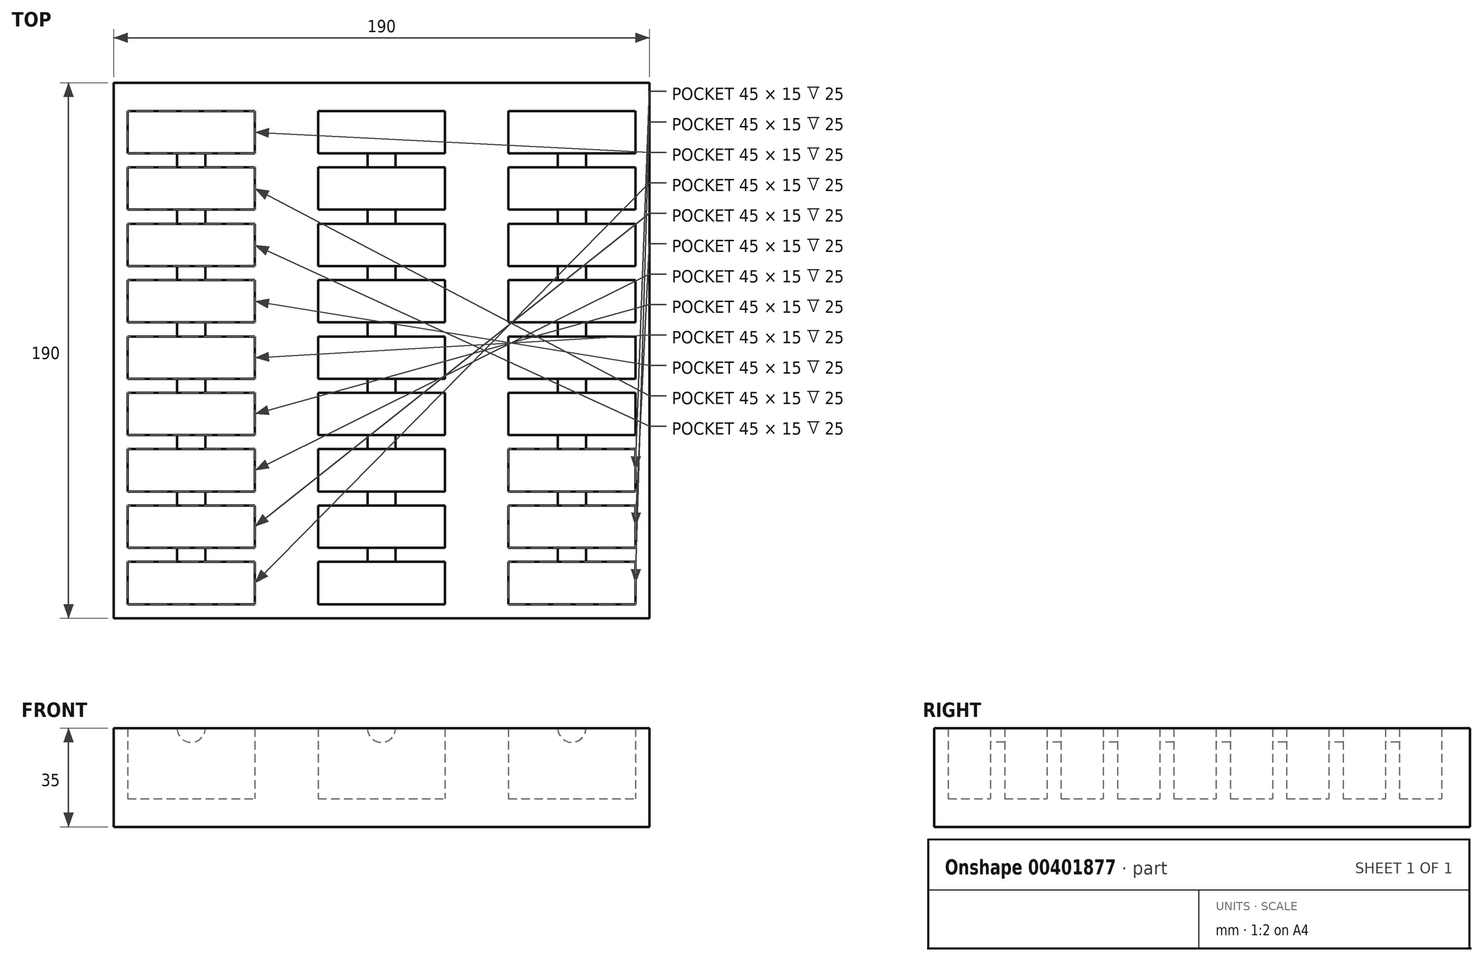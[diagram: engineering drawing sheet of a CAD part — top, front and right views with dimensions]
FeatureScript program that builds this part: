
annotation { "Feature Type Name" : "Feature", "Feature Type Description" : "" }
export const myFeature = defineFeature(function(context is Context, id is Id, definition is map)
    precondition{}
    {
        {
            var Q0;
            Q0=qCreatedBy(makeId("Top.planeOp"),FACE);
            var sketch = newSketch(context, id + "F0", { "sketchPlane" : qUnion([Q0])});
            skLineSegment(sketch, "E0.bottom", {"start": v(-95, 95) * mm, "end": v(95, 95) * mm});
            skLineSegment(sketch, "E0.top", {"start": v(-95, -95) * mm, "end": v(95, -95) * mm});
            skLineSegment(sketch, "E0.left", {"start": v(-95, 95) * mm, "end": v(-95, -95) * mm});
            skLineSegment(sketch, "E0.right", {"start": v(95, 95) * mm, "end": v(95, -95) * mm});
            skPoint(sketch, "E0.middle", {"position": v(0, 0) * mm});
            skSolve(sketch);
        }
        {
            var Q0;
            Q0 = qSketchRegion(id + "F0", true);
            extrude(context, id + "F1", {"entities" : qUnion([Q0]), "depth" : 35 * mm});
        }
        {
            var Q0;
            Q0=makeQuery(id+"F1.opExtrude","CAP_FACE",FACE,{"disambiguationData":[OSD([sQuery(id+"F0.wireOp",EDGE,"E0.bottom"),sQuery(id+"F0.wireOp",EDGE,"E0.top"),sQuery(id+"F0.wireOp",EDGE,"E0.left"),sQuery(id+"F0.wireOp",EDGE,"E0.right")])],"isStart":false});
            var sketch = newSketch(context, id + "F2", { "sketchPlane" : qUnion([Q0])});
            skLineSegment(sketch, "E1.bottom", {"start": v(90, 90) * mm, "end": v(-90, 90) * mm});
            skLineSegment(sketch, "E1.top", {"start": v(90, -90) * mm, "end": v(-90, -90) * mm});
            skLineSegment(sketch, "E1.left", {"start": v(90, 90) * mm, "end": v(90, -90) * mm});
            skLineSegment(sketch, "E1.right", {"start": v(-90, 90) * mm, "end": v(-90, -90) * mm});
            skPoint(sketch, "E1.middle", {"position": v(0, 0) * mm});
            skSolve(sketch);
        }
        {
            var Q0;
            Q0 = qSketchRegion(id + "F2", true);
            extrude(context, id + "F3", {"entities" : qUnion([Q0]), "operationType" : NewBodyOperationType.REMOVE, "oppositeDirection" : true, "depth" : 25 * mm});
        }
        {
            var Q0;
            Q0=makeQuery(id+"F3.boolean.opBoolean","COPY",FACE,{"derivedFrom":makeQuery(id+"F3.opExtrude","CAP_FACE",FACE,{"disambiguationData":[OSD([sQuery(id+"F2.wireOp",EDGE,"E1.bottom"),sQuery(id+"F2.wireOp",EDGE,"E1.top"),sQuery(id+"F2.wireOp",EDGE,"E1.left"),sQuery(id+"F2.wireOp",EDGE,"E1.right")])],"isStart":false})});
            var sketch = newSketch(context, id + "F4", { "sketchPlane" : qUnion([Q0])});
            skLineSegment(sketch, "E2.top", {"start": v(-90, -75) * mm, "end": v(-45, -75) * mm});
            skLineSegment(sketch, "E2.right", {"start": v(-45, -90) * mm, "end": v(-45, -75) * mm});
            skLineSegment(sketch, "E3.0", {"start": v(-40, -90) * mm, "end": v(-40, -70) * mm});
            skLineSegment(sketch, "E3.1", {"start": v(-90, -70) * mm, "end": v(-40, -70) * mm});
            skLineSegment(sketch, "E4", {"start": v(-45, -90) * mm, "end": v(-40, -90) * mm});
            skLineSegment(sketch, "E5", {"start": v(-90, -75) * mm, "end": v(-90, -70) * mm});
            skLineSegment(sketch, "E6", {"start": v(-45, -70) * mm, "end": v(-45, -55) * mm});
            skLineSegment(sketch, "E7", {"start": v(-45, -55) * mm, "end": v(-90, -55) * mm});
            skLineSegment(sketch, "E8.0", {"start": v(-40, -50) * mm, "end": v(-90, -50) * mm});
            skLineSegment(sketch, "E8.1", {"start": v(-40, -70) * mm, "end": v(-40, -50) * mm});
            skLineSegment(sketch, "E9", {"start": v(-90, -50) * mm, "end": v(-90, -55) * mm});
            skLineSegment(sketch, "E10", {"start": v(-45, -50) * mm, "end": v(-45, -35) * mm});
            skLineSegment(sketch, "E11", {"start": v(-45, -35) * mm, "end": v(-90, -35) * mm});
            skLineSegment(sketch, "E12.0", {"start": v(-40, -30) * mm, "end": v(-90, -30) * mm});
            skLineSegment(sketch, "E12.1", {"start": v(-40, -50) * mm, "end": v(-40, -30) * mm});
            skLineSegment(sketch, "E13", {"start": v(-90, -30) * mm, "end": v(-90, -35) * mm});
            skLineSegment(sketch, "E14", {"start": v(-45, -30) * mm, "end": v(-45, -15) * mm});
            skLineSegment(sketch, "E15", {"start": v(-45, -15) * mm, "end": v(-90, -15) * mm});
            skLineSegment(sketch, "E16.0", {"start": v(-40, -10) * mm, "end": v(-90, -10) * mm});
            skLineSegment(sketch, "E16.1", {"start": v(-40, -30) * mm, "end": v(-40, -10) * mm});
            skLineSegment(sketch, "E17", {"start": v(-90, -10) * mm, "end": v(-90, -15) * mm});
            skLineSegment(sketch, "E18", {"start": v(-45, -10) * mm, "end": v(-45, 5) * mm});
            skLineSegment(sketch, "E19", {"start": v(-45, 5) * mm, "end": v(-90, 5) * mm});
            skLineSegment(sketch, "E20.0", {"start": v(-40, 10) * mm, "end": v(-90, 10) * mm});
            skLineSegment(sketch, "E20.1", {"start": v(-40, -10) * mm, "end": v(-40, 10) * mm});
            skLineSegment(sketch, "E21", {"start": v(-90, 10) * mm, "end": v(-90, 5) * mm});
            skLineSegment(sketch, "E22", {"start": v(-45, 10) * mm, "end": v(-45, 25) * mm});
            skLineSegment(sketch, "E23", {"start": v(-45, 25) * mm, "end": v(-90, 25) * mm});
            skLineSegment(sketch, "E24.0", {"start": v(-40, 30) * mm, "end": v(-90, 30) * mm});
            skLineSegment(sketch, "E24.1", {"start": v(-40, 10) * mm, "end": v(-40, 30) * mm});
            skLineSegment(sketch, "E25", {"start": v(-90, 30) * mm, "end": v(-90, 25) * mm});
            skLineSegment(sketch, "E26", {"start": v(-45, 30) * mm, "end": v(-45, 45) * mm});
            skLineSegment(sketch, "E27", {"start": v(-45, 45) * mm, "end": v(-90, 45) * mm});
            skLineSegment(sketch, "E28.0", {"start": v(-40, 50) * mm, "end": v(-90, 50) * mm});
            skLineSegment(sketch, "E28.1", {"start": v(-40, 30) * mm, "end": v(-40, 50) * mm});
            skLineSegment(sketch, "E29", {"start": v(-90, 50) * mm, "end": v(-90, 45) * mm});
            skLineSegment(sketch, "E30", {"start": v(-45, 50) * mm, "end": v(-45, 65) * mm});
            skLineSegment(sketch, "E31", {"start": v(-45, 65) * mm, "end": v(-90, 65) * mm});
            skLineSegment(sketch, "E32.0", {"start": v(-40, 70) * mm, "end": v(-90, 70) * mm});
            skLineSegment(sketch, "E32.1", {"start": v(-40, 50) * mm, "end": v(-40, 70) * mm});
            skLineSegment(sketch, "E33", {"start": v(-90, 70) * mm, "end": v(-90, 65) * mm});
            skLineSegment(sketch, "E34", {"start": v(-45, 70) * mm, "end": v(-45, 85) * mm});
            skLineSegment(sketch, "E35", {"start": v(-45, 85) * mm, "end": v(-90, 85) * mm});
            skLineSegment(sketch, "E36", {"start": v(-40, 70) * mm, "end": v(-40, 90) * mm});
            skLineSegment(sketch, "E37", {"start": v(-40, 90) * mm, "end": v(-90, 90) * mm});
            skLineSegment(sketch, "E38", {"start": v(-90, 90) * mm, "end": v(-90, 85) * mm});
            skLineSegment(sketch, "E39.MirrorCS", {"start": v(40, 70) * mm, "end": v(40, 90) * mm});
            skLineSegment(sketch, "E40.MirrorCS", {"start": v(40, 90) * mm, "end": v(90, 90) * mm});
            skLineSegment(sketch, "E41.MirrorCS", {"start": v(90, 90) * mm, "end": v(90, 85) * mm});
            skLineSegment(sketch, "E42.MirrorCS", {"start": v(45, 85) * mm, "end": v(90, 85) * mm});
            skLineSegment(sketch, "E43.MirrorCS", {"start": v(45, 70) * mm, "end": v(45, 85) * mm});
            skLineSegment(sketch, "E44.MirrorCS", {"start": v(40, 70) * mm, "end": v(90, 70) * mm});
            skLineSegment(sketch, "E45.MirrorCS", {"start": v(90, 70) * mm, "end": v(90, 65) * mm});
            skLineSegment(sketch, "E46.MirrorCS", {"start": v(45, 65) * mm, "end": v(90, 65) * mm});
            skLineSegment(sketch, "E47.MirrorCS", {"start": v(40, 50) * mm, "end": v(40, 70) * mm});
            skLineSegment(sketch, "E48.MirrorCS", {"start": v(40, 50) * mm, "end": v(90, 50) * mm});
            skLineSegment(sketch, "E49.MirrorCS", {"start": v(45, 50) * mm, "end": v(45, 65) * mm});
            skLineSegment(sketch, "E50.MirrorCS", {"start": v(40, 30) * mm, "end": v(40, 50) * mm});
            skLineSegment(sketch, "E51.MirrorCS", {"start": v(40, 10) * mm, "end": v(40, 30) * mm});
            skLineSegment(sketch, "E52.MirrorCS", {"start": v(40, -10) * mm, "end": v(40, 10) * mm});
            skLineSegment(sketch, "E53.MirrorCS", {"start": v(40, -30) * mm, "end": v(40, -10) * mm});
            skLineSegment(sketch, "E54.MirrorCS", {"start": v(40, -50) * mm, "end": v(40, -30) * mm});
            skLineSegment(sketch, "E55.MirrorCS", {"start": v(40, -70) * mm, "end": v(40, -50) * mm});
            skLineSegment(sketch, "E56.MirrorCS", {"start": v(40, -90) * mm, "end": v(40, -70) * mm});
            skLineSegment(sketch, "E57.MirrorCS", {"start": v(45, -90) * mm, "end": v(45, -75) * mm});
            skLineSegment(sketch, "E58.MirrorCS", {"start": v(45, -70) * mm, "end": v(45, -55) * mm});
            skLineSegment(sketch, "E59.MirrorCS", {"start": v(45, -50) * mm, "end": v(45, -35) * mm});
            skLineSegment(sketch, "E60.MirrorCS", {"start": v(45, -30) * mm, "end": v(45, -15) * mm});
            skLineSegment(sketch, "E61.MirrorCS", {"start": v(45, -10) * mm, "end": v(45, 5) * mm});
            skLineSegment(sketch, "E62.MirrorCS", {"start": v(45, 10) * mm, "end": v(45, 25) * mm});
            skLineSegment(sketch, "E63.MirrorCS", {"start": v(45, 30) * mm, "end": v(45, 45) * mm});
            skLineSegment(sketch, "E64.MirrorCS", {"start": v(45, 45) * mm, "end": v(90, 45) * mm});
            skLineSegment(sketch, "E65.MirrorCS", {"start": v(40, 30) * mm, "end": v(90, 30) * mm});
            skLineSegment(sketch, "E66.MirrorCS", {"start": v(45, 25) * mm, "end": v(90, 25) * mm});
            skLineSegment(sketch, "E67.MirrorCS", {"start": v(40, 10) * mm, "end": v(90, 10) * mm});
            skLineSegment(sketch, "E68.MirrorCS", {"start": v(45, 5) * mm, "end": v(90, 5) * mm});
            skLineSegment(sketch, "E69.MirrorCS", {"start": v(40, -10) * mm, "end": v(90, -10) * mm});
            skLineSegment(sketch, "E70.MirrorCS", {"start": v(45, -15) * mm, "end": v(90, -15) * mm});
            skLineSegment(sketch, "E71.MirrorCS", {"start": v(40, -30) * mm, "end": v(90, -30) * mm});
            skLineSegment(sketch, "E72.MirrorCS", {"start": v(45, -35) * mm, "end": v(90, -35) * mm});
            skLineSegment(sketch, "E73.MirrorCS", {"start": v(40, -50) * mm, "end": v(90, -50) * mm});
            skLineSegment(sketch, "E74.MirrorCS", {"start": v(45, -55) * mm, "end": v(90, -55) * mm});
            skLineSegment(sketch, "E75.MirrorCS", {"start": v(90, -70) * mm, "end": v(40, -70) * mm});
            skLineSegment(sketch, "E76.MirrorCS", {"start": v(90, -75) * mm, "end": v(45, -75) * mm});
            skLineSegment(sketch, "E77.MirrorCS", {"start": v(45, -90) * mm, "end": v(40, -90) * mm});
            skLineSegment(sketch, "E78.MirrorCS", {"start": v(90, -75) * mm, "end": v(90, -70) * mm});
            skLineSegment(sketch, "E79.MirrorCS", {"start": v(90, -50) * mm, "end": v(90, -55) * mm});
            skLineSegment(sketch, "E80.MirrorCS", {"start": v(90, -30) * mm, "end": v(90, -35) * mm});
            skLineSegment(sketch, "E81.MirrorCS", {"start": v(90, -10) * mm, "end": v(90, -15) * mm});
            skLineSegment(sketch, "E82.MirrorCS", {"start": v(90, 10) * mm, "end": v(90, 5) * mm});
            skLineSegment(sketch, "E83.MirrorCS", {"start": v(90, 30) * mm, "end": v(90, 25) * mm});
            skLineSegment(sketch, "E84.MirrorCS", {"start": v(90, 50) * mm, "end": v(90, 45) * mm});
            skSolve(sketch);
        }
        {
            var Q0;
            Q0 = qSketchRegion(id + "F4", true);
            extrude(context, id + "F5", {"entities" : qUnion([Q0]), "operationType" : NewBodyOperationType.ADD, "depth" : 25 * mm});
        }
        {
            var Q0;
            {var subQ0=sQuery(id+"F2.wireOp",EDGE,"E1.bottom");var subQ1=sQuery(id+"F2.wireOp",EDGE,"E1.top");Q0=makeQuery(id+"F5.boolean.opBoolean","SPLIT",FACE,{"disambiguationData":[TD([makeQuery(id+"F3.boolean.opBoolean","COPY",FACE,{"derivedFrom":makeQuery(id+"F3.opExtrude","SWEPT_FACE",FACE,{"disambiguationData":[OSD([subQ0])]})})])],"derivedFrom":makeQuery(id+"F3.boolean.opBoolean","COPY",FACE,{"derivedFrom":makeQuery(id+"F3.opExtrude","CAP_FACE",FACE,{"disambiguationData":[OSD([subQ0,subQ1,sQuery(id+"F2.wireOp",EDGE,"E1.left"),sQuery(id+"F2.wireOp",EDGE,"E1.right")])],"isStart":false})})});}
            var sketch = newSketch(context, id + "F6", { "sketchPlane" : qUnion([Q0])});
            skLineSegment(sketch, "E85", {"start": v(-22.5, -90) * mm, "end": v(22.5, -90) * mm});
            skLineSegment(sketch, "E86.top", {"start": v(-22.5, -75) * mm, "end": v(22.5, -75) * mm});
            skLineSegment(sketch, "E86.left", {"start": v(-22.5, -90) * mm, "end": v(-22.5, -75) * mm});
            skLineSegment(sketch, "E86.right", {"start": v(22.5, -90) * mm, "end": v(22.5, -75) * mm});
            skLineSegment(sketch, "E87", {"start": v(-22.5, -75) * mm, "end": v(-22.5, 90) * mm});
            skLineSegment(sketch, "E88", {"start": v(22.5, -75) * mm, "end": v(22.5, 90) * mm});
            skLineSegment(sketch, "E89", {"start": v(22.5, 90) * mm, "end": v(-22.5, 90) * mm});
            skLineSegment(sketch, "E90", {"start": v(-22.5, 90) * mm, "end": v(-40, 90) * mm});
            skLineSegment(sketch, "E91", {"start": v(-40, 90) * mm, "end": v(-40, -90) * mm});
            skLineSegment(sketch, "E92", {"start": v(-40, -90) * mm, "end": v(-22.5, -90) * mm});
            skLineSegment(sketch, "E93", {"start": v(22.5, -90) * mm, "end": v(40, -90) * mm});
            skLineSegment(sketch, "E94", {"start": v(22.5, 90) * mm, "end": v(40, 90) * mm});
            skLineSegment(sketch, "E95", {"start": v(40, 90) * mm, "end": v(40, -90) * mm});
            skSolve(sketch);
        }
        {
            var Q0;
            Q0=makeQuery(id+"F6.imprint","IMPRINT",FACE,{"disambiguationData":[TD([[makeQuery(id+"F6.imprint","IMPRINT",EDGE,{"derivedFrom":sQuery(id+"F6.wireOp",EDGE,"E86.left")}),1.0]])]});
            var Q1;
            Q1=makeQuery(id+"F6.imprint","IMPRINT",FACE,{"disambiguationData":[TD([[makeQuery(id+"F6.imprint","IMPRINT",EDGE,{"derivedFrom":sQuery(id+"F6.wireOp",EDGE,"E86.right")}),-1.0]])]});
            extrude(context, id + "F7", {"entities" : qUnion([Q0, Q1]), "operationType" : NewBodyOperationType.ADD, "depth" : 25 * mm});
        }
        {
            var Q0;
            {var subQ0=sQuery(id+"F2.wireOp",EDGE,"E1.bottom");var subQ1=sQuery(id+"F2.wireOp",EDGE,"E1.top");Q0=makeQuery(id+"F5.boolean.opBoolean","SPLIT",FACE,{"disambiguationData":[TD([makeQuery(id+"F3.boolean.opBoolean","COPY",FACE,{"derivedFrom":makeQuery(id+"F3.opExtrude","SWEPT_FACE",FACE,{"disambiguationData":[OSD([subQ0])]})})])],"derivedFrom":makeQuery(id+"F3.boolean.opBoolean","COPY",FACE,{"derivedFrom":makeQuery(id+"F3.opExtrude","CAP_FACE",FACE,{"disambiguationData":[OSD([subQ0,subQ1,sQuery(id+"F2.wireOp",EDGE,"E1.left"),sQuery(id+"F2.wireOp",EDGE,"E1.right")])],"isStart":false})})});}
            var sketch = newSketch(context, id + "F8", { "sketchPlane" : qUnion([Q0])});
            skLineSegment(sketch, "E96", {"start": v(22.5, -75) * mm, "end": v(22.5, -70) * mm});
            skLineSegment(sketch, "E97", {"start": v(22.5, -70) * mm, "end": v(-22.5, -70) * mm});
            skLineSegment(sketch, "E98", {"start": v(-22.5, -70) * mm, "end": v(-22.5, -75) * mm});
            skLineSegment(sketch, "E99", {"start": v(-22.5, -75) * mm, "end": v(22.5, -75) * mm});
            skLineSegment(sketch, "E100.bottom", {"start": v(-22.5, -55) * mm, "end": v(22.5, -55) * mm});
            skLineSegment(sketch, "E100.top", {"start": v(-22.5, -50) * mm, "end": v(22.5, -50) * mm});
            skLineSegment(sketch, "E100.left", {"start": v(-22.5, -55) * mm, "end": v(-22.5, -50) * mm});
            skLineSegment(sketch, "E100.right", {"start": v(22.5, -55) * mm, "end": v(22.5, -50) * mm});
            skLineSegment(sketch, "E101.bottom", {"start": v(-22.5, -35) * mm, "end": v(22.5, -35) * mm});
            skLineSegment(sketch, "E101.top", {"start": v(-22.5, -30) * mm, "end": v(22.5, -30) * mm});
            skLineSegment(sketch, "E101.left", {"start": v(-22.5, -35) * mm, "end": v(-22.5, -30) * mm});
            skLineSegment(sketch, "E101.right", {"start": v(22.5, -35) * mm, "end": v(22.5, -30) * mm});
            skLineSegment(sketch, "E102.bottom", {"start": v(-22.5, -15) * mm, "end": v(22.5, -15) * mm});
            skLineSegment(sketch, "E102.top", {"start": v(-22.5, -10) * mm, "end": v(22.5, -10) * mm});
            skLineSegment(sketch, "E102.left", {"start": v(-22.5, -15) * mm, "end": v(-22.5, -10) * mm});
            skLineSegment(sketch, "E102.right", {"start": v(22.5, -15) * mm, "end": v(22.5, -10) * mm});
            skLineSegment(sketch, "E103.bottom", {"start": v(-22.5, 5) * mm, "end": v(22.5, 5) * mm});
            skLineSegment(sketch, "E103.top", {"start": v(-22.5, 10) * mm, "end": v(22.5, 10) * mm});
            skLineSegment(sketch, "E103.left", {"start": v(-22.5, 5) * mm, "end": v(-22.5, 10) * mm});
            skLineSegment(sketch, "E103.right", {"start": v(22.5, 5) * mm, "end": v(22.5, 10) * mm});
            skLineSegment(sketch, "E104.bottom", {"start": v(-22.5, 25) * mm, "end": v(22.5, 25) * mm});
            skLineSegment(sketch, "E104.top", {"start": v(-22.5, 30) * mm, "end": v(22.5, 30) * mm});
            skLineSegment(sketch, "E104.left", {"start": v(-22.5, 25) * mm, "end": v(-22.5, 30) * mm});
            skLineSegment(sketch, "E104.right", {"start": v(22.5, 25) * mm, "end": v(22.5, 30) * mm});
            skLineSegment(sketch, "E105.bottom", {"start": v(-22.5, 45) * mm, "end": v(22.5, 45) * mm});
            skLineSegment(sketch, "E105.top", {"start": v(-22.5, 50) * mm, "end": v(22.5, 50) * mm});
            skLineSegment(sketch, "E105.left", {"start": v(-22.5, 45) * mm, "end": v(-22.5, 50) * mm});
            skLineSegment(sketch, "E105.right", {"start": v(22.5, 45) * mm, "end": v(22.5, 50) * mm});
            skLineSegment(sketch, "E106.bottom", {"start": v(-22.5, 65) * mm, "end": v(22.5, 65) * mm});
            skLineSegment(sketch, "E106.top", {"start": v(-22.5, 70) * mm, "end": v(22.5, 70) * mm});
            skLineSegment(sketch, "E106.left", {"start": v(-22.5, 65) * mm, "end": v(-22.5, 70) * mm});
            skLineSegment(sketch, "E106.right", {"start": v(22.5, 65) * mm, "end": v(22.5, 70) * mm});
            skLineSegment(sketch, "E107.bottom", {"start": v(-22.5, 85) * mm, "end": v(22.5, 85) * mm});
            skLineSegment(sketch, "E107.top", {"start": v(-22.5, 90) * mm, "end": v(22.5, 90) * mm});
            skLineSegment(sketch, "E107.left", {"start": v(-22.5, 85) * mm, "end": v(-22.5, 90) * mm});
            skLineSegment(sketch, "E107.right", {"start": v(22.5, 85) * mm, "end": v(22.5, 90) * mm});
            skSolve(sketch);
        }
        {
            var Q0;
            Q0 = qSketchRegion(id + "F8", true);
            extrude(context, id + "F9", {"entities" : qUnion([Q0]), "operationType" : NewBodyOperationType.ADD, "depth" : 25 * mm});
        }
        {
            var Q0;
            Q0=makeQuery(id+"F5.opExtrude","SWEPT_FACE",FACE,{"disambiguationData":[OSD([sQuery(id+"F4.wireOp",EDGE,"E2.top")])]});
            var sketch = newSketch(context, id + "F10", { "sketchPlane" : qUnion([Q0])});
            skCircle(sketch, "E108", {"center": v(-67.5, 35) * mm, "radius": 5 * mm});
            skSolve(sketch);
        }
        {
            var Q0;
            Q0 = qSketchRegion(id + "F10", true);
            extrude(context, id + "F11", {"entities" : qUnion([Q0]), "operationType" : NewBodyOperationType.REMOVE, "oppositeDirection" : true, "depth" : 152 * mm});
        }
        {
            var Q0;
            Q0=makeQuery(id+"F9.opExtrude","SWEPT_FACE",FACE,{"disambiguationData":[OSD([sQuery(id+"F8.wireOp",EDGE,"E99")])]});
            var sketch = newSketch(context, id + "F12", { "sketchPlane" : qUnion([Q0])});
            skCircle(sketch, "E109", {"center": v(0, 35) * mm, "radius": 5 * mm});
            skSolve(sketch);
        }
        {
            var Q0;
            Q0 = qSketchRegion(id + "F12", true);
            extrude(context, id + "F13", {"entities" : qUnion([Q0]), "operationType" : NewBodyOperationType.REMOVE, "oppositeDirection" : true, "depth" : 145 * mm});
        }
        {
            var Q0;
            Q0=makeQuery(id+"F5.opExtrude","SWEPT_FACE",FACE,{"disambiguationData":[OSD([sQuery(id+"F4.wireOp",EDGE,"E76.MirrorCS")])]});
            var sketch = newSketch(context, id + "F14", { "sketchPlane" : qUnion([Q0])});
            skCircle(sketch, "E110", {"center": v(67.5, 35) * mm, "radius": 5 * mm});
            skSolve(sketch);
        }
        {
            var Q0;
            Q0 = qSketchRegion(id + "F14", true);
            extrude(context, id + "F15", {"entities" : qUnion([Q0]), "operationType" : NewBodyOperationType.REMOVE, "oppositeDirection" : true, "depth" : 145 * mm});
        }
    });
